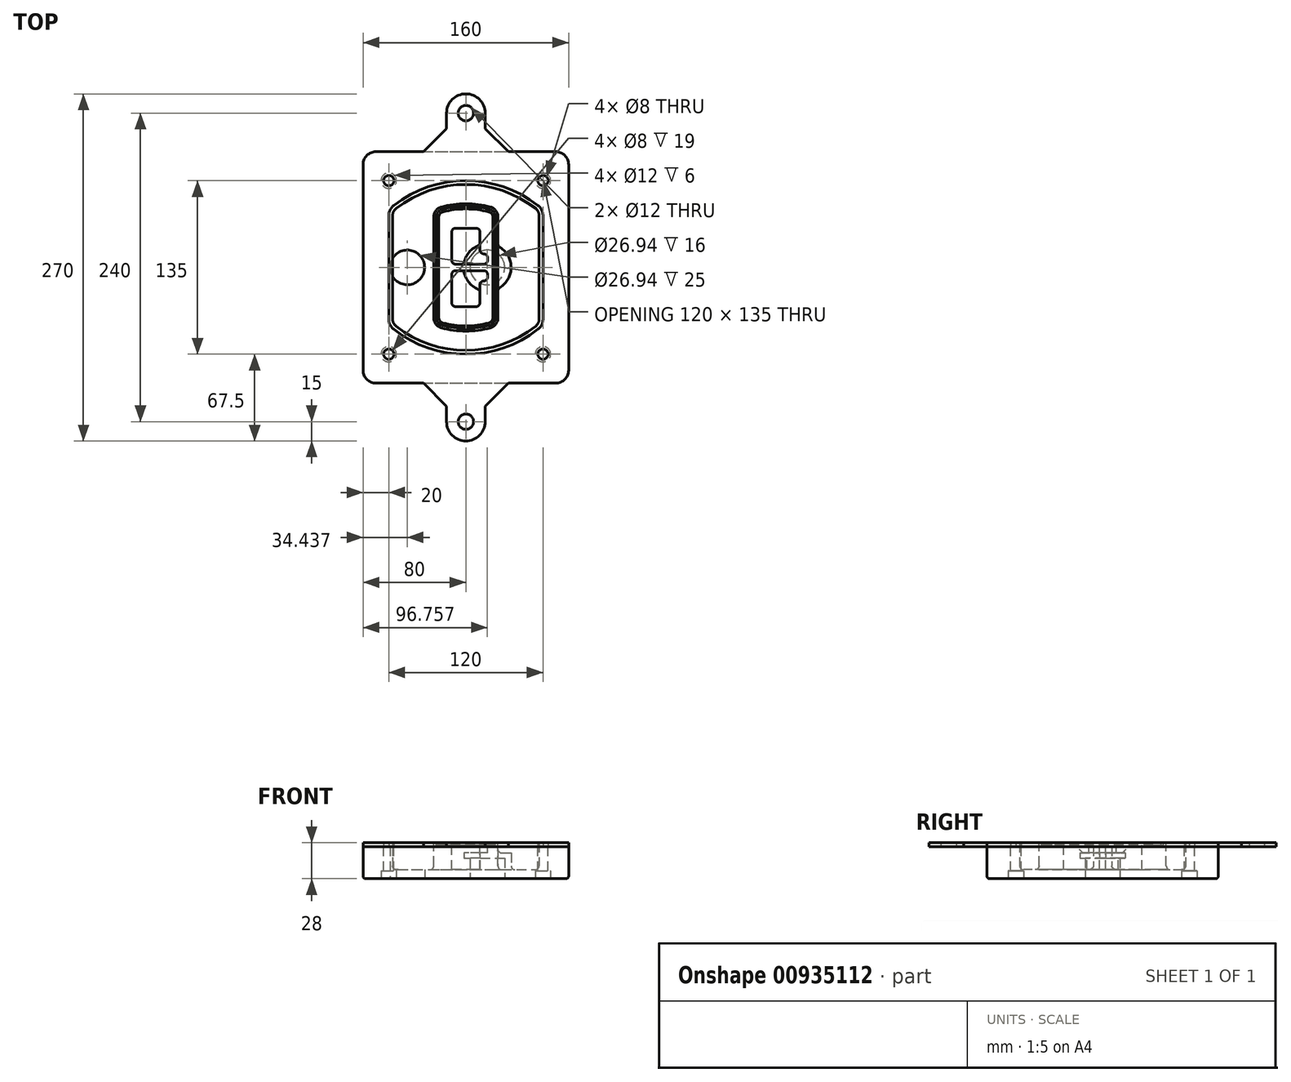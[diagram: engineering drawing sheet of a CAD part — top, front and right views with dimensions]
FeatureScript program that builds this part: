
annotation { "Feature Type Name" : "Feature", "Feature Type Description" : "" }
export const myFeature = defineFeature(function(context is Context, id is Id, definition is map)
    precondition{}
    {
        {
            var Q0;
            Q0=qCreatedBy(makeId("Top.planeOp"),FACE);
            var sketch = newSketch(context, id + "F0", { "sketchPlane" : qUnion([Q0])});
            skPoint(sketch, "E0.rect.middle", {"position": v(0, 0) * mm});
            skLineSegment(sketch, "E1.bottom", {"start": v(-70, -90) * mm, "end": v(70, -90) * mm});
            skLineSegment(sketch, "E1.top", {"start": v(-70, 90) * mm, "end": v(70, 90) * mm});
            skLineSegment(sketch, "E1.left", {"start": v(-80, -80) * mm, "end": v(-80, 80) * mm});
            skLineSegment(sketch, "E1.right", {"start": v(80, -80) * mm, "end": v(80, 80) * mm});
            skLineSegment(sketch, "E2", {"start": v(-80, 90) * mm, "end": v(80, -90) * mm, "construction": true});
            skLineSegment(sketch, "E3", {"start": v(80, 90) * mm, "end": v(-80, -90) * mm, "construction": true});
            skCircle(sketch, "E4", {"center": v(-60, 67.5) * mm, "radius": 4 * mm});
            skCircle(sketch, "E5", {"center": v(60, 67.5) * mm, "radius": 4 * mm});
            skCircle(sketch, "E6", {"center": v(60, -67.5) * mm, "radius": 4 * mm});
            skCircle(sketch, "E7", {"center": v(-60, -67.5) * mm, "radius": 4 * mm});
            skLineSegment(sketch, "E8", {"start": v(-60, 67.5) * mm, "end": v(60, 67.5) * mm, "construction": true});
            skLineSegment(sketch, "E9", {"start": v(60, 67.5) * mm, "end": v(60, -67.5) * mm, "construction": true});
            skLineSegment(sketch, "E10", {"start": v(60, -67.5) * mm, "end": v(-60, -67.5) * mm, "construction": true});
            skLineSegment(sketch, "E11", {"start": v(-60, -67.5) * mm, "end": v(-60, 67.5) * mm, "construction": true});
            skLineSegment(sketch, "E12", {"start": v(-60, 40.3) * mm, "end": v(-60, -40.3) * mm});
            skLineSegment(sketch, "E13", {"start": v(60, 40.3) * mm, "end": v(60, -40.3) * mm});
            skArc(sketch, "E14", {"start": v(56.15, 48.18) * mm, "mid": v(0, 67.5) * mm, "end": v(-56.15, 48.18) * mm});
            skArc(sketch, "E15", {"start": v(-56.15, -48.18) * mm, "mid": v(0, -67.5) * mm, "end": v(56.15, -48.18) * mm});
            skLineSegment(sketch, "E16", {"start": v(-60, 0) * mm, "end": v(60, 0) * mm, "construction": true});
            skPoint(sketch, "E17.visualSharp", {"position": v(-60, -45) * mm});
            skArc(sketch, "E17.filletArc", {"start": v(-60, -40.3) * mm, "mid": v(-58.99, -44.68) * mm, "end": v(-56.15, -48.18) * mm});
            skPoint(sketch, "E18.visualSharp", {"position": v(-60, 45) * mm});
            skArc(sketch, "E18.filletArc", {"start": v(-56.15, 48.18) * mm, "mid": v(-58.99, 44.68) * mm, "end": v(-60, 40.3) * mm});
            skPoint(sketch, "E19.visualSharp", {"position": v(60, 45) * mm});
            skArc(sketch, "E19.filletArc", {"start": v(60, 40.3) * mm, "mid": v(58.99, 44.68) * mm, "end": v(56.15, 48.18) * mm});
            skPoint(sketch, "E20.visualSharp", {"position": v(60, -45) * mm});
            skArc(sketch, "E20.filletArc", {"start": v(56.15, -48.18) * mm, "mid": v(58.99, -44.68) * mm, "end": v(60, -40.3) * mm});
            skPoint(sketch, "E21.visualSharp", {"position": v(-80, 90) * mm});
            skArc(sketch, "E21.filletArc", {"start": v(-70, 90) * mm, "mid": v(-77.07, 87.07) * mm, "end": v(-80, 80) * mm});
            skPoint(sketch, "E22.visualSharp", {"position": v(80, 90) * mm});
            skArc(sketch, "E22.filletArc", {"start": v(80, 80) * mm, "mid": v(77.07, 87.07) * mm, "end": v(70, 90) * mm});
            skPoint(sketch, "E23.visualSharp", {"position": v(80, -90) * mm});
            skArc(sketch, "E23.filletArc", {"start": v(70, -90) * mm, "mid": v(77.07, -87.07) * mm, "end": v(80, -80) * mm});
            skPoint(sketch, "E24.visualSharp", {"position": v(-80, -90) * mm});
            skArc(sketch, "E24.filletArc", {"start": v(-80, -80) * mm, "mid": v(-77.07, -87.07) * mm, "end": v(-70, -90) * mm});
            skArc(sketch, "E25.0", {"start": v(57, 40.3) * mm, "mid": v(56.3, 43.36) * mm, "end": v(54.3, 45.81) * mm});
            skLineSegment(sketch, "E25.1", {"start": v(57, 40.3) * mm, "end": v(57, -40.3) * mm});
            skArc(sketch, "E25.2", {"start": v(54.3, -45.81) * mm, "mid": v(56.3, -43.36) * mm, "end": v(57, -40.3) * mm});
            skArc(sketch, "E25.3", {"start": v(-54.3, -45.81) * mm, "mid": v(0, -64.5) * mm, "end": v(54.3, -45.81) * mm});
            skArc(sketch, "E25.4", {"start": v(-57, -40.3) * mm, "mid": v(-56.3, -43.36) * mm, "end": v(-54.3, -45.81) * mm});
            skArc(sketch, "E25.5", {"start": v(54.3, 45.81) * mm, "mid": v(0, 64.5) * mm, "end": v(-54.3, 45.81) * mm});
            skLineSegment(sketch, "E25.6", {"start": v(-57, 40.3) * mm, "end": v(-57, -40.3) * mm});
            skArc(sketch, "E25.7", {"start": v(-54.3, 45.81) * mm, "mid": v(-56.3, 43.36) * mm, "end": v(-57, 40.3) * mm});
            skArc(sketch, "E26.0", {"start": v(-58.62, 51.33) * mm, "mid": v(-62.58, 46.43) * mm, "end": v(-64, 40.3) * mm});
            skArc(sketch, "E26.1", {"start": v(58.62, 51.33) * mm, "mid": v(0, 71.5) * mm, "end": v(-58.62, 51.33) * mm});
            skArc(sketch, "E26.2", {"start": v(64, 40.3) * mm, "mid": v(62.58, 46.43) * mm, "end": v(58.62, 51.33) * mm});
            skLineSegment(sketch, "E26.3", {"start": v(64, 40.3) * mm, "end": v(64, -40.3) * mm});
            skArc(sketch, "E26.4", {"start": v(58.62, -51.33) * mm, "mid": v(62.58, -46.43) * mm, "end": v(64, -40.3) * mm});
            skLineSegment(sketch, "E26.5", {"start": v(-64, 40.3) * mm, "end": v(-64, -40.3) * mm});
            skArc(sketch, "E26.6", {"start": v(-58.62, -51.33) * mm, "mid": v(0, -71.5) * mm, "end": v(58.62, -51.33) * mm});
            skArc(sketch, "E26.7", {"start": v(-64, -40.3) * mm, "mid": v(-62.58, -46.43) * mm, "end": v(-58.62, -51.33) * mm});
            skSolve(sketch);
        }
        {
            var Q0;
            Q0=makeQuery(id+"F0.imprint","IMPRINT",FACE,{"disambiguationData":[TD([[makeQuery(id+"F0.imprint","IMPRINT",EDGE,{"derivedFrom":sQuery(id+"F0.wireOp",EDGE,"E1.bottom")}),1.0]])]});
            var Q1;
            Q1=makeQuery(id+"F0.imprint","IMPRINT",FACE,{"disambiguationData":[TD([[makeQuery(id+"F0.imprint","IMPRINT",EDGE,{"derivedFrom":sQuery(id+"F0.wireOp",EDGE,"E12")}),1.0]])]});
            var Q2;
            Q2=makeQuery(id+"F0.imprint","IMPRINT",FACE,{"disambiguationData":[TD([[makeQuery(id+"F0.imprint","IMPRINT",EDGE,{"derivedFrom":sQuery(id+"F0.wireOp",EDGE,"E25.0")}),1.0]])]});
            var Q3;
            Q3=makeQuery(id+"F0.imprint","IMPRINT",FACE,{"disambiguationData":[TD([[makeQuery(id+"F0.imprint","IMPRINT",EDGE,{"derivedFrom":sQuery(id+"F0.wireOp",EDGE,"E12")}),-1.0]])]});
            extrude(context, id + "F1", {"entities" : qUnion([Q0, Q1, Q2, Q3]), "oppositeDirection" : true, "depth" : 25 * mm, "offsetDistance" : 25 * mm});
        }
        {
            var Q0;
            Q0=makeQuery(id+"F0.imprint","IMPRINT",FACE,{"disambiguationData":[TD([[makeQuery(id+"F0.imprint","IMPRINT",EDGE,{"derivedFrom":sQuery(id+"F0.wireOp",EDGE,"E12")}),1.0]])]});
            extrude(context, id + "F2", {"entities" : qUnion([Q0]), "operationType" : NewBodyOperationType.ADD, "depth" : 3 * mm});
        }
        {
            var Q0;
            Q0=makeQuery(id+"F0.imprint","IMPRINT",FACE,{"disambiguationData":[TD([[makeQuery(id+"F0.imprint","IMPRINT",EDGE,{"derivedFrom":sQuery(id+"F0.wireOp",EDGE,"E25.0")}),1.0]])]});
            extrude(context, id + "F3", {"entities" : qUnion([Q0]), "operationType" : NewBodyOperationType.REMOVE, "oppositeDirection" : true, "depth" : 18 * mm});
        }
        {
            var Q0;
            Q0=makeQuery(id+"F2.opExtrude","CAP_FACE",FACE,{"disambiguationData":[OSD([sQuery(id+"F0.wireOp",EDGE,"E12"),sQuery(id+"F0.wireOp",EDGE,"E13"),sQuery(id+"F0.wireOp",EDGE,"E14"),sQuery(id+"F0.wireOp",EDGE,"E15"),sQuery(id+"F0.wireOp",EDGE,"E17.filletArc"),sQuery(id+"F0.wireOp",EDGE,"E18.filletArc"),sQuery(id+"F0.wireOp",EDGE,"E19.filletArc"),sQuery(id+"F0.wireOp",EDGE,"E20.filletArc"),sQuery(id+"F0.wireOp",EDGE,"E25.0"),sQuery(id+"F0.wireOp",EDGE,"E25.1"),sQuery(id+"F0.wireOp",EDGE,"E25.2"),sQuery(id+"F0.wireOp",EDGE,"E25.3"),sQuery(id+"F0.wireOp",EDGE,"E25.4"),sQuery(id+"F0.wireOp",EDGE,"E25.5"),sQuery(id+"F0.wireOp",EDGE,"E25.6"),sQuery(id+"F0.wireOp",EDGE,"E25.7")])],"isStart":false});
            var sketch = newSketch(context, id + "F4", { "sketchPlane" : qUnion([Q0])});
            skArc(sketch, "E27.0", {"start": v(-19.08, -46.97) * mm, "mid": v(0, -49.5) * mm, "end": v(19.08, -46.97) * mm});
            skArc(sketch, "E28.0", {"start": v(19.08, 46.97) * mm, "mid": v(0, 49.5) * mm, "end": v(-19.08, 46.97) * mm});
            skLineSegment(sketch, "E29", {"start": v(-25, 39.25) * mm, "end": v(-25, -39.25) * mm});
            skLineSegment(sketch, "E30", {"start": v(25, 39.25) * mm, "end": v(25, -39.25) * mm});
            skLineSegment(sketch, "E31", {"start": v(-25, 45.1) * mm, "end": v(25, 45.1) * mm, "construction": true});
            skLineSegment(sketch, "E32", {"start": v(-25, -45.1) * mm, "end": v(25, -45.1) * mm, "construction": true});
            skPoint(sketch, "E33.visualSharp", {"position": v(-25, 45.1) * mm});
            skArc(sketch, "E33.filletArc", {"start": v(-19.08, 46.97) * mm, "mid": v(-23.35, 44.11) * mm, "end": v(-25, 39.25) * mm});
            skPoint(sketch, "E34.visualSharp", {"position": v(25, 45.1) * mm});
            skArc(sketch, "E34.filletArc", {"start": v(25, 39.25) * mm, "mid": v(23.35, 44.11) * mm, "end": v(19.08, 46.97) * mm});
            skPoint(sketch, "E35.visualSharp", {"position": v(25, -45.1) * mm});
            skArc(sketch, "E35.filletArc", {"start": v(19.08, -46.97) * mm, "mid": v(23.35, -44.11) * mm, "end": v(25, -39.25) * mm});
            skPoint(sketch, "E36.visualSharp", {"position": v(-25, -45.1) * mm});
            skArc(sketch, "E36.filletArc", {"start": v(-25, -39.25) * mm, "mid": v(-23.35, -44.11) * mm, "end": v(-19.08, -46.97) * mm});
            skArc(sketch, "E37.0", {"start": v(54.3, 45.81) * mm, "mid": v(0, 64.5) * mm, "end": v(-54.3, 45.81) * mm});
            skArc(sketch, "E37.1", {"start": v(-54.3, 45.81) * mm, "mid": v(-56.3, 43.36) * mm, "end": v(-57, 40.3) * mm});
            skLineSegment(sketch, "E37.2", {"start": v(-57, 40.3) * mm, "end": v(-57, -40.3) * mm});
            skArc(sketch, "E37.3", {"start": v(-57, -40.3) * mm, "mid": v(-56.3, -43.36) * mm, "end": v(-54.3, -45.81) * mm});
            skArc(sketch, "E37.4", {"start": v(-54.3, -45.81) * mm, "mid": v(0, -64.5) * mm, "end": v(54.3, -45.81) * mm});
            skArc(sketch, "E37.5", {"start": v(54.3, -45.81) * mm, "mid": v(56.3, -43.36) * mm, "end": v(57, -40.3) * mm});
            skLineSegment(sketch, "E37.6", {"start": v(57, 40.3) * mm, "end": v(57, -40.3) * mm});
            skArc(sketch, "E37.7", {"start": v(57, 40.3) * mm, "mid": v(56.3, 43.36) * mm, "end": v(54.3, 45.81) * mm});
            skLineSegment(sketch, "E38.0", {"start": v(23, 39.25) * mm, "end": v(23, -39.25) * mm});
            skArc(sketch, "E38.1", {"start": v(18.56, -45.04) * mm, "mid": v(21.76, -42.9) * mm, "end": v(23, -39.25) * mm});
            skArc(sketch, "E38.2", {"start": v(-18.56, -45.04) * mm, "mid": v(0, -47.5) * mm, "end": v(18.56, -45.04) * mm});
            skArc(sketch, "E38.3", {"start": v(-23, -39.25) * mm, "mid": v(-21.76, -42.9) * mm, "end": v(-18.56, -45.04) * mm});
            skLineSegment(sketch, "E38.4", {"start": v(-23, 39.25) * mm, "end": v(-23, -39.25) * mm});
            skArc(sketch, "E38.5", {"start": v(23, 39.25) * mm, "mid": v(21.76, 42.9) * mm, "end": v(18.56, 45.04) * mm});
            skArc(sketch, "E38.6", {"start": v(-18.56, 45.04) * mm, "mid": v(-21.76, 42.9) * mm, "end": v(-23, 39.25) * mm});
            skArc(sketch, "E38.7", {"start": v(18.56, 45.04) * mm, "mid": v(0, 47.5) * mm, "end": v(-18.56, 45.04) * mm});
            skArc(sketch, "E39.0", {"start": v(21, 39.25) * mm, "mid": v(20.18, 41.68) * mm, "end": v(18.04, 43.1) * mm});
            skLineSegment(sketch, "E39.1", {"start": v(21, 39.25) * mm, "end": v(21, -39.25) * mm});
            skArc(sketch, "E39.2", {"start": v(18.04, -43.1) * mm, "mid": v(20.18, -41.68) * mm, "end": v(21, -39.25) * mm});
            skArc(sketch, "E39.3", {"start": v(-18.04, -43.1) * mm, "mid": v(0, -45.5) * mm, "end": v(18.04, -43.1) * mm});
            skArc(sketch, "E39.4", {"start": v(-21, -39.25) * mm, "mid": v(-20.18, -41.68) * mm, "end": v(-18.04, -43.1) * mm});
            skArc(sketch, "E39.5", {"start": v(18.04, 43.1) * mm, "mid": v(0, 45.5) * mm, "end": v(-18.04, 43.1) * mm});
            skLineSegment(sketch, "E39.6", {"start": v(-21, 39.25) * mm, "end": v(-21, -39.25) * mm});
            skArc(sketch, "E39.7", {"start": v(-18.04, 43.1) * mm, "mid": v(-20.18, 41.68) * mm, "end": v(-21, 39.25) * mm});
            skLineSegment(sketch, "E40", {"start": v(-25, 0) * mm, "end": v(25, 0) * mm, "construction": true});
            skLineSegment(sketch, "E41", {"start": v(-11, 5.5) * mm, "end": v(-11, 27.5) * mm});
            skLineSegment(sketch, "E42", {"start": v(-8, 30.5) * mm, "end": v(8, 30.5) * mm});
            skLineSegment(sketch, "E43", {"start": v(11, 27.5) * mm, "end": v(11, 13.5) * mm});
            skLineSegment(sketch, "E44", {"start": v(14, 10.5) * mm, "end": v(14, 10.5) * mm});
            skLineSegment(sketch, "E45", {"start": v(17, 7.5) * mm, "end": v(17, 5.5) * mm});
            skLineSegment(sketch, "E46", {"start": v(14, 2.5) * mm, "end": v(-8, 2.5) * mm});
            skPoint(sketch, "E47.visualSharp", {"position": v(-11, 30.5) * mm});
            skArc(sketch, "E47.filletArc", {"start": v(-8, 30.5) * mm, "mid": v(-10.12, 29.62) * mm, "end": v(-11, 27.5) * mm});
            skPoint(sketch, "E48.visualSharp", {"position": v(11, 30.5) * mm});
            skArc(sketch, "E48.filletArc", {"start": v(11, 27.5) * mm, "mid": v(10.12, 29.62) * mm, "end": v(8, 30.5) * mm});
            skPoint(sketch, "E49.visualSharp", {"position": v(11, 10.5) * mm});
            skArc(sketch, "E49.filletArc", {"start": v(11, 13.5) * mm, "mid": v(11.88, 11.38) * mm, "end": v(14, 10.5) * mm});
            skPoint(sketch, "E50.visualSharp", {"position": v(17, 10.5) * mm});
            skArc(sketch, "E50.filletArc", {"start": v(17, 7.5) * mm, "mid": v(16.12, 9.62) * mm, "end": v(14, 10.5) * mm});
            skPoint(sketch, "E51.visualSharp", {"position": v(17, 2.5) * mm});
            skArc(sketch, "E51.filletArc", {"start": v(14, 2.5) * mm, "mid": v(16.12, 3.38) * mm, "end": v(17, 5.5) * mm});
            skPoint(sketch, "E52.visualSharp", {"position": v(-11, 2.5) * mm});
            skArc(sketch, "E52.filletArc", {"start": v(-11, 5.5) * mm, "mid": v(-10.12, 3.38) * mm, "end": v(-8, 2.5) * mm});
            skLineSegment(sketch, "E53.0.MirrorCS", {"start": v(14, -2.5) * mm, "end": v(-8, -2.5) * mm});
            skArc(sketch, "E54.0.MirrorCS", {"start": v(-11, -5.5) * mm, "mid": v(-10.12, -3.38) * mm, "end": v(-8, -2.5) * mm});
            skLineSegment(sketch, "E55.0.MirrorCS", {"start": v(-11, -5.5) * mm, "end": v(-11, -27.5) * mm});
            skArc(sketch, "E56.0.MirrorCS", {"start": v(-8, -30.5) * mm, "mid": v(-10.12, -29.62) * mm, "end": v(-11, -27.5) * mm});
            skLineSegment(sketch, "E57.0.MirrorCS", {"start": v(-8, -30.5) * mm, "end": v(8, -30.5) * mm});
            skArc(sketch, "E58.0.MirrorCS", {"start": v(11, -27.5) * mm, "mid": v(10.12, -29.62) * mm, "end": v(8, -30.5) * mm});
            skLineSegment(sketch, "E59.0.MirrorCS", {"start": v(11, -27.5) * mm, "end": v(11, -13.5) * mm});
            skArc(sketch, "E60.0.MirrorCS", {"start": v(11, -13.5) * mm, "mid": v(11.88, -11.38) * mm, "end": v(14, -10.5) * mm});
            skArc(sketch, "E61.0.MirrorCS", {"start": v(17, -7.5) * mm, "mid": v(16.12, -9.62) * mm, "end": v(14, -10.5) * mm});
            skLineSegment(sketch, "E62.0.MirrorCS", {"start": v(17, -7.5) * mm, "end": v(17, -5.5) * mm});
            skArc(sketch, "E63.0.MirrorCS", {"start": v(14, -2.5) * mm, "mid": v(16.12, -3.38) * mm, "end": v(17, -5.5) * mm});
            skSolve(sketch);
        }
        {
            var Q0;
            Q0=makeQuery(id+"F4.imprint","IMPRINT",FACE,{"disambiguationData":[TD([[makeQuery(id+"F4.imprint","IMPRINT",EDGE,{"derivedFrom":sQuery(id+"F4.wireOp",EDGE,"E27.0")}),1.0]])]});
            var Q1;
            Q1=makeQuery(id+"F4.imprint","IMPRINT",FACE,{"disambiguationData":[TD([[makeQuery(id+"F4.imprint","IMPRINT",EDGE,{"derivedFrom":sQuery(id+"F4.wireOp",EDGE,"E38.0")}),-1.0]])]});
            var Q2;
            Q2=makeQuery(id+"F4.imprint","IMPRINT",FACE,{"disambiguationData":[TD([[makeQuery(id+"F4.imprint","IMPRINT",EDGE,{"derivedFrom":sQuery(id+"F4.wireOp",EDGE,"E39.0")}),1.0]])]});
            extrude(context, id + "F5", {"entities" : qUnion([Q0, Q1, Q2]), "operationType" : NewBodyOperationType.ADD, "endBound" : BoundingType.UP_TO_NEXT, "oppositeDirection" : true, "depth" : 25 * mm});
        }
        {
            var Q0;
            Q0=makeQuery(id+"F4.imprint","IMPRINT",FACE,{"disambiguationData":[TD([[makeQuery(id+"F4.imprint","IMPRINT",EDGE,{"derivedFrom":sQuery(id+"F4.wireOp",EDGE,"E38.0")}),-1.0]])]});
            extrude(context, id + "F6", {"entities" : qUnion([Q0]), "operationType" : NewBodyOperationType.REMOVE, "oppositeDirection" : true, "depth" : 2 * mm});
        }
        {
            var Q0;
            Q0=makeQuery(id+"F1.opExtrude","CAP_FACE",FACE,{"disambiguationData":[OSD([sQuery(id+"F0.wireOp",EDGE,"E1.bottom"),sQuery(id+"F0.wireOp",EDGE,"E1.top"),sQuery(id+"F0.wireOp",EDGE,"E1.left"),sQuery(id+"F0.wireOp",EDGE,"E1.right"),sQuery(id+"F0.wireOp",EDGE,"E4"),sQuery(id+"F0.wireOp",EDGE,"E5"),sQuery(id+"F0.wireOp",EDGE,"E6"),sQuery(id+"F0.wireOp",EDGE,"E7"),sQuery(id+"F0.wireOp",EDGE,"E21.filletArc"),sQuery(id+"F0.wireOp",EDGE,"E22.filletArc"),sQuery(id+"F0.wireOp",EDGE,"E23.filletArc"),sQuery(id+"F0.wireOp",EDGE,"E24.filletArc")])],"isStart":false});
            var sketch = newSketch(context, id + "F7", { "sketchPlane" : qUnion([Q0])});
            skCircle(sketch, "E64", {"center": v(16.76, 0) * mm, "radius": 13.47 * mm});
            skCircle(sketch, "E65", {"center": v(-45.56, 0) * mm, "radius": 13.47 * mm});
            skLineSegment(sketch, "E66", {"start": v(80, 0) * mm, "end": v(-80, 0) * mm});
            skCircle(sketch, "E67", {"center": v(16.76, 0) * mm, "radius": 18.47 * mm});
            skCircle(sketch, "E68", {"center": v(60, -67.5) * mm, "radius": 6 * mm});
            skCircle(sketch, "E69", {"center": v(-60, -67.5) * mm, "radius": 6 * mm});
            skCircle(sketch, "E70", {"center": v(-60, 67.5) * mm, "radius": 6 * mm});
            skCircle(sketch, "E71", {"center": v(60, 67.5) * mm, "radius": 6 * mm});
            skSolve(sketch);
        }
        {
            var Q0;
            {var subQ1=sQuery(id+"F7.wireOp",EDGE,"E66");var subQ4=sQuery(id+"F7.wireOp",EDGE,"E64");var subQ6=makeQuery(id+"F7.imprint","INTERSECT",VERTEX,{"disambiguationData":[OD(0.0)],"derivedFrom":[subQ4,subQ1]});Q0=makeQuery(id+"F7.imprint","IMPRINT",FACE,{"disambiguationData":[TD([[makeQuery(id+"F7.imprint","IMPRINT",EDGE,{"disambiguationData":[TD([[subQ6,-1.0]])],"derivedFrom":subQ4}),-1.0]])]});}
            var Q1;
            {var subQ0=sQuery(id+"F7.wireOp",EDGE,"E66");var subQ1=sQuery(id+"F7.wireOp",EDGE,"E64");var subQ3=makeQuery(id+"F7.imprint","INTERSECT",VERTEX,{"disambiguationData":[OD(0.0)],"derivedFrom":[subQ1,subQ0]});Q1=makeQuery(id+"F7.imprint","IMPRINT",FACE,{"disambiguationData":[TD([[makeQuery(id+"F7.imprint","IMPRINT",EDGE,{"disambiguationData":[TD([[subQ3,-1.0]])],"derivedFrom":subQ1}),1.0]])]});}
            var Q2;
            {var subQ0=sQuery(id+"F7.wireOp",EDGE,"E66");var subQ1=sQuery(id+"F7.wireOp",EDGE,"E64");var subQ3=makeQuery(id+"F7.imprint","INTERSECT",VERTEX,{"disambiguationData":[OD(0.0)],"derivedFrom":[subQ1,subQ0]});Q2=makeQuery(id+"F7.imprint","IMPRINT",FACE,{"disambiguationData":[TD([[makeQuery(id+"F7.imprint","IMPRINT",EDGE,{"disambiguationData":[TD([[subQ3,1.0]])],"derivedFrom":subQ1}),1.0]])]});}
            var Q3;
            {var subQ1=sQuery(id+"F7.wireOp",EDGE,"E66");var subQ4=sQuery(id+"F7.wireOp",EDGE,"E64");var subQ6=makeQuery(id+"F7.imprint","INTERSECT",VERTEX,{"disambiguationData":[OD(0.0)],"derivedFrom":[subQ4,subQ1]});Q3=makeQuery(id+"F7.imprint","IMPRINT",FACE,{"disambiguationData":[TD([[makeQuery(id+"F7.imprint","IMPRINT",EDGE,{"disambiguationData":[TD([[subQ6,1.0]])],"derivedFrom":subQ4}),-1.0]])]});}
            extrude(context, id + "F8", {"entities" : qUnion([Q0, Q1, Q2, Q3]), "operationType" : NewBodyOperationType.ADD, "oppositeDirection" : true, "depth" : 20 * mm});
        }
        {
            var Q0;
            {var subQ0=sQuery(id+"F7.wireOp",EDGE,"E66");var subQ1=sQuery(id+"F7.wireOp",EDGE,"E64");var subQ3=makeQuery(id+"F7.imprint","INTERSECT",VERTEX,{"disambiguationData":[OD(0.0)],"derivedFrom":[subQ1,subQ0]});Q0=makeQuery(id+"F7.imprint","IMPRINT",FACE,{"disambiguationData":[TD([[makeQuery(id+"F7.imprint","IMPRINT",EDGE,{"disambiguationData":[TD([[subQ3,-1.0]])],"derivedFrom":subQ1}),1.0]])]});}
            var Q1;
            {var subQ0=sQuery(id+"F7.wireOp",EDGE,"E66");var subQ1=sQuery(id+"F7.wireOp",EDGE,"E64");var subQ3=makeQuery(id+"F7.imprint","INTERSECT",VERTEX,{"disambiguationData":[OD(0.0)],"derivedFrom":[subQ1,subQ0]});Q1=makeQuery(id+"F7.imprint","IMPRINT",FACE,{"disambiguationData":[TD([[makeQuery(id+"F7.imprint","IMPRINT",EDGE,{"disambiguationData":[TD([[subQ3,1.0]])],"derivedFrom":subQ1}),1.0]])]});}
            extrude(context, id + "F9", {"entities" : qUnion([Q0, Q1]), "operationType" : NewBodyOperationType.REMOVE, "oppositeDirection" : true, "depth" : 16 * mm});
        }
        {
            var Q0;
            {var subQ0=sQuery(id+"F7.wireOp",EDGE,"E66");var subQ1=sQuery(id+"F7.wireOp",EDGE,"E65");var subQ3=makeQuery(id+"F7.imprint","INTERSECT",VERTEX,{"disambiguationData":[OD(0.0)],"derivedFrom":[subQ1,subQ0]});Q0=makeQuery(id+"F7.imprint","IMPRINT",FACE,{"disambiguationData":[TD([[makeQuery(id+"F7.imprint","IMPRINT",EDGE,{"disambiguationData":[TD([[subQ3,-1.0]])],"derivedFrom":subQ1}),1.0]])]});}
            var Q1;
            {var subQ0=sQuery(id+"F7.wireOp",EDGE,"E66");var subQ1=sQuery(id+"F7.wireOp",EDGE,"E65");var subQ3=makeQuery(id+"F7.imprint","INTERSECT",VERTEX,{"disambiguationData":[OD(0.0)],"derivedFrom":[subQ1,subQ0]});Q1=makeQuery(id+"F7.imprint","IMPRINT",FACE,{"disambiguationData":[TD([[makeQuery(id+"F7.imprint","IMPRINT",EDGE,{"disambiguationData":[TD([[subQ3,1.0]])],"derivedFrom":subQ1}),1.0]])]});}
            extrude(context, id + "F10", {"entities" : qUnion([Q0, Q1]), "operationType" : NewBodyOperationType.REMOVE, "oppositeDirection" : true, "depth" : 25 * mm});
        }
        {
            var Q0;
            Q0=makeQuery(id+"F7.imprint","IMPRINT",FACE,{"disambiguationData":[TD([[makeQuery(id+"F7.imprint","IMPRINT",EDGE,{"derivedFrom":sQuery(id+"F7.wireOp",EDGE,"E68")}),1.0]])]});
            var Q1;
            Q1=makeQuery(id+"F7.imprint","IMPRINT",FACE,{"disambiguationData":[TD([[makeQuery(id+"F7.imprint","IMPRINT",EDGE,{"derivedFrom":makeQuery(id+"F1.opExtrude","CAP_EDGE",EDGE,{"disambiguationData":[OSD([sQuery(id+"F0.wireOp",EDGE,"E5")])],"isStart":false})}),-1.0]])]});
            var Q2;
            Q2=makeQuery(id+"F7.imprint","IMPRINT",FACE,{"disambiguationData":[TD([[makeQuery(id+"F7.imprint","IMPRINT",EDGE,{"derivedFrom":sQuery(id+"F7.wireOp",EDGE,"E69")}),1.0]])]});
            var Q3;
            Q3=makeQuery(id+"F7.imprint","IMPRINT",FACE,{"disambiguationData":[TD([[makeQuery(id+"F7.imprint","IMPRINT",EDGE,{"derivedFrom":makeQuery(id+"F1.opExtrude","CAP_EDGE",EDGE,{"disambiguationData":[OSD([sQuery(id+"F0.wireOp",EDGE,"E4")])],"isStart":false})}),-1.0]])]});
            var Q4;
            Q4=makeQuery(id+"F7.imprint","IMPRINT",FACE,{"disambiguationData":[TD([[makeQuery(id+"F7.imprint","IMPRINT",EDGE,{"derivedFrom":sQuery(id+"F7.wireOp",EDGE,"E70")}),1.0]])]});
            var Q5;
            Q5=makeQuery(id+"F7.imprint","IMPRINT",FACE,{"disambiguationData":[TD([[makeQuery(id+"F7.imprint","IMPRINT",EDGE,{"derivedFrom":makeQuery(id+"F1.opExtrude","CAP_EDGE",EDGE,{"disambiguationData":[OSD([sQuery(id+"F0.wireOp",EDGE,"E7")])],"isStart":false})}),-1.0]])]});
            var Q6;
            Q6=makeQuery(id+"F7.imprint","IMPRINT",FACE,{"disambiguationData":[TD([[makeQuery(id+"F7.imprint","IMPRINT",EDGE,{"derivedFrom":sQuery(id+"F7.wireOp",EDGE,"E71")}),1.0]])]});
            var Q7;
            Q7=makeQuery(id+"F7.imprint","IMPRINT",FACE,{"disambiguationData":[TD([[makeQuery(id+"F7.imprint","IMPRINT",EDGE,{"derivedFrom":makeQuery(id+"F1.opExtrude","CAP_EDGE",EDGE,{"disambiguationData":[OSD([sQuery(id+"F0.wireOp",EDGE,"E6")])],"isStart":false})}),-1.0]])]});
            extrude(context, id + "F11", {"entities" : qUnion([Q0, Q1, Q2, Q3, Q4, Q5, Q6, Q7]), "operationType" : NewBodyOperationType.REMOVE, "oppositeDirection" : true, "depth" : 6 * mm});
        }
        {
            var Q0;
            Q0=makeQuery(id+"F9.boolean.opBoolean","COPY",FACE,{"derivedFrom":makeQuery(id+"F9.opExtrude","CAP_FACE",FACE,{"disambiguationData":[OSD([sQuery(id+"F7.wireOp",EDGE,"E64")])],"isStart":false})});
            var sketch = newSketch(context, id + "F12", { "sketchPlane" : qUnion([Q0])});
            skArc(sketch, "E72.0", {"start": v(11, 17.55) * mm, "mid": v(2.57, 11.82) * mm, "end": v(-1.54, 2.5) * mm});
            skArc(sketch, "E72.1", {"start": v(-1.54, -2.5) * mm, "mid": v(2.57, -11.82) * mm, "end": v(11, -17.55) * mm});
            skLineSegment(sketch, "E73", {"start": v(-1.54, -2.5) * mm, "end": v(14, -2.5) * mm});
            skLineSegment(sketch, "E74.0", {"start": v(14, 2.5) * mm, "end": v(-1.54, 2.5) * mm});
            skArc(sketch, "E74.1", {"start": v(14, 2.5) * mm, "mid": v(16.12, 3.38) * mm, "end": v(17, 5.5) * mm});
            skLineSegment(sketch, "E74.2", {"start": v(17, 7.5) * mm, "end": v(17, 5.5) * mm});
            skArc(sketch, "E74.3", {"start": v(17, 7.5) * mm, "mid": v(16.12, 9.62) * mm, "end": v(14, 10.5) * mm});
            skArc(sketch, "E74.4", {"start": v(11, 13.5) * mm, "mid": v(11.88, 11.38) * mm, "end": v(14, 10.5) * mm});
            skLineSegment(sketch, "E74.5", {"start": v(11, 17.55) * mm, "end": v(11, 13.5) * mm});
            skLineSegment(sketch, "E74.7", {"start": v(14, -2.5) * mm, "end": v(-1.54, -2.5) * mm});
            skArc(sketch, "E74.8", {"start": v(14, -2.5) * mm, "mid": v(16.12, -3.38) * mm, "end": v(17, -5.5) * mm});
            skLineSegment(sketch, "E74.9", {"start": v(17, -7.5) * mm, "end": v(17, -5.5) * mm});
            skArc(sketch, "E74.10", {"start": v(17, -7.5) * mm, "mid": v(16.12, -9.62) * mm, "end": v(14, -10.5) * mm});
            skArc(sketch, "E74.11", {"start": v(11, -13.5) * mm, "mid": v(11.88, -11.38) * mm, "end": v(14, -10.5) * mm});
            skLineSegment(sketch, "E74.12", {"start": v(11, -17.55) * mm, "end": v(11, -13.5) * mm});
            skPoint(sketch, "E75.orphan", {"position": v(11, -27.5) * mm});
            skPoint(sketch, "E76.orphan", {"position": v(-8, -2.5) * mm});
            skPoint(sketch, "E77.orphan", {"position": v(-8, 2.5) * mm});
            skPoint(sketch, "E78.orphan", {"position": v(11, 27.5) * mm});
            skSolve(sketch);
        }
        {
            var Q0;
            {var subQ7=sQuery(id+"F12.wireOp",EDGE,"E72.0");var subQ14=sQuery(id+"F12.wireOp",EDGE,"E72.1");var subQ16=sQuery(id+"F12.wireOp",EDGE,"E74.1");var subQ18=sQuery(id+"F12.wireOp",EDGE,"E74.8");Q0=qUnion([makeQuery(id+"F12.imprint","IMPRINT",FACE,{"disambiguationData":[TD([[makeQuery(id+"F12.imprint","IMPRINT",EDGE,{"derivedFrom":subQ7}),1.0]])]}),makeQuery(id+"F12.imprint","IMPRINT",FACE,{"disambiguationData":[TD([[makeQuery(id+"F12.imprint","IMPRINT",EDGE,{"derivedFrom":subQ14}),1.0]])]}),makeQuery(id+"F12.imprint","IMPRINT",FACE,{"disambiguationData":[TD([[makeQuery(id+"F12.imprint","IMPRINT",EDGE,{"derivedFrom":subQ16}),1.0]])]}),makeQuery(id+"F12.imprint","IMPRINT",FACE,{"disambiguationData":[TD([[makeQuery(id+"F12.imprint","IMPRINT",EDGE,{"derivedFrom":subQ18}),-1.0]])]})]);}
            var Q1;
            Q1=makeQuery(id+"F5.boolean.opBoolean","SPLIT",FACE,{"disambiguationData":[TD([makeQuery(id+"F5.opExtrude","SWEPT_FACE",FACE,{"disambiguationData":[OSD([sQuery(id+"F4.wireOp",EDGE,"E41")])]})])],"derivedFrom":makeQuery(id+"F3.boolean.opBoolean","COPY",FACE,{"derivedFrom":makeQuery(id+"F3.opExtrude","CAP_FACE",FACE,{"disambiguationData":[OSD([sQuery(id+"F0.wireOp",EDGE,"E25.0"),sQuery(id+"F0.wireOp",EDGE,"E25.1"),sQuery(id+"F0.wireOp",EDGE,"E25.2"),sQuery(id+"F0.wireOp",EDGE,"E25.3"),sQuery(id+"F0.wireOp",EDGE,"E25.4"),sQuery(id+"F0.wireOp",EDGE,"E25.5"),sQuery(id+"F0.wireOp",EDGE,"E25.6"),sQuery(id+"F0.wireOp",EDGE,"E25.7")])],"isStart":false})})});
            extrude(context, id + "F13", {"entities" : qUnion([Q0]), "operationType" : NewBodyOperationType.REMOVE, "endBound" : BoundingType.UP_TO_SURFACE, "endBoundEntityFace" : qUnion([Q1]), "depth" : 25 * mm});
        }
        {
            var Q0;
            Q0=makeQuery(id+"F3.boolean.opBoolean","COPY",EDGE,{"derivedFrom":makeQuery(id+"F3.opExtrude","CAP_EDGE",EDGE,{"disambiguationData":[OSD([sQuery(id+"F0.wireOp",EDGE,"E25.6")])],"isStart":false})});
            var Q1;
            Q1=makeQuery(id+"F8.boolean.opBoolean","INTERSECT",EDGE,{"derivedFrom":[makeQuery(id+"F5.opExtrude","SWEPT_FACE",FACE,{"disambiguationData":[OSD([sQuery(id+"F4.wireOp",EDGE,"E30")])]}),makeQuery(id+"F8.opExtrude","CAP_FACE",FACE,{"disambiguationData":[OSD([sQuery(id+"F7.wireOp",EDGE,"E67")])],"isStart":false})]});
            var Q2;
            Q2=makeQuery(id+"F8.boolean.opBoolean","INTERSECT",EDGE,{"disambiguationData":[OD(1.0)],"derivedFrom":[makeQuery(id+"F5.opExtrude","SWEPT_FACE",FACE,{"disambiguationData":[OSD([sQuery(id+"F4.wireOp",EDGE,"E30")])]}),makeQuery(id+"F8.opExtrude","SWEPT_FACE",FACE,{"disambiguationData":[OSD([sQuery(id+"F7.wireOp",EDGE,"E67")])]})]});
            var Q3;
            {var subQ0=sQuery(id+"F4.wireOp",EDGE,"E30");Q3=makeQuery(id+"F8.boolean.opBoolean","SPLIT",EDGE,{"disambiguationData":[TD([makeQuery(id+"F5.opExtrude","SWEPT_FACE",FACE,{"disambiguationData":[OSD([sQuery(id+"F4.wireOp",EDGE,"E35.filletArc")])]})])],"derivedFrom":makeQuery(id+"F5.opExtrude","CAP_EDGE",EDGE,{"disambiguationData":[OSD([subQ0])],"isStart":false})});}
            var Q4;
            {var subQ0=sQuery(id+"F0.wireOp",EDGE,"E25.7");var subQ1=sQuery(id+"F0.wireOp",EDGE,"E25.1");var subQ2=sQuery(id+"F0.wireOp",EDGE,"E25.6");var subQ3=sQuery(id+"F0.wireOp",EDGE,"E25.5");var subQ4=sQuery(id+"F0.wireOp",EDGE,"E25.4");var subQ5=sQuery(id+"F0.wireOp",EDGE,"E25.0");var subQ6=sQuery(id+"F0.wireOp",EDGE,"E25.2");var subQ7=sQuery(id+"F0.wireOp",EDGE,"E25.3");Q4=makeQuery(id+"F8.boolean.opBoolean","INTERSECT",EDGE,{"derivedFrom":[makeQuery(id+"F5.boolean.opBoolean","SPLIT",FACE,{"disambiguationData":[TD([makeQuery(id+"F2.opExtrude","SWEPT_FACE",FACE,{"disambiguationData":[OSD([subQ5])]})])],"derivedFrom":makeQuery(id+"F3.boolean.opBoolean","COPY",FACE,{"derivedFrom":makeQuery(id+"F3.opExtrude","CAP_FACE",FACE,{"disambiguationData":[OSD([subQ5,subQ1,subQ6,subQ7,subQ4,subQ3,subQ2,subQ0])],"isStart":false})})}),makeQuery(id+"F8.opExtrude","SWEPT_FACE",FACE,{"disambiguationData":[OSD([sQuery(id+"F7.wireOp",EDGE,"E67")])]})]});}
            var Q5;
            Q5=makeQuery(id+"F8.boolean.opBoolean","INTERSECT",EDGE,{"disambiguationData":[OD(0.0)],"derivedFrom":[makeQuery(id+"F5.opExtrude","SWEPT_FACE",FACE,{"disambiguationData":[OSD([sQuery(id+"F4.wireOp",EDGE,"E30")])]}),makeQuery(id+"F8.opExtrude","SWEPT_FACE",FACE,{"disambiguationData":[OSD([sQuery(id+"F7.wireOp",EDGE,"E67")])]})]});
            fillet(context, id + "F14", {"entities" : qUnion([Q0, Q1, Q2, Q3, Q4, Q5]), "radius" : 3 * mm, "tangentPropagation" : true, "allowEdgeOverflow" : false});
        }
        {
            var Q0;
            Q0=makeQuery(id+"F1.opExtrude","CAP_EDGE",EDGE,{"disambiguationData":[OSD([sQuery(id+"F0.wireOp",EDGE,"E1.bottom")])],"isStart":false});
            fillet(context, id + "F15", {"entities" : qUnion([Q0]), "radius" : 2 * mm, "tangentPropagation" : true, "allowEdgeOverflow" : false});
        }
        {
            var Q0;
            {var subQ0=sQuery(id+"F0.wireOp",EDGE,"E21.filletArc");var subQ1=sQuery(id+"F0.wireOp",EDGE,"E7");var subQ2=sQuery(id+"F0.wireOp",EDGE,"E6");var subQ3=sQuery(id+"F0.wireOp",EDGE,"E5");var subQ4=sQuery(id+"F0.wireOp",EDGE,"E4");var subQ5=sQuery(id+"F0.wireOp",EDGE,"E22.filletArc");var subQ6=sQuery(id+"F0.wireOp",EDGE,"E1.bottom");var subQ7=sQuery(id+"F0.wireOp",EDGE,"E1.right");var subQ8=sQuery(id+"F0.wireOp",EDGE,"E1.top");var subQ9=sQuery(id+"F0.wireOp",EDGE,"E1.left");var subQ10=sQuery(id+"F0.wireOp",EDGE,"E23.filletArc");var subQ11=sQuery(id+"F0.wireOp",EDGE,"E24.filletArc");Q0=makeQuery(id+"F2.boolean.opBoolean","SPLIT",FACE,{"disambiguationData":[TD([makeQuery(id+"F1.opExtrude","SWEPT_FACE",FACE,{"disambiguationData":[OSD([subQ6])]})])],"derivedFrom":makeQuery(id+"F1.opExtrude","CAP_FACE",FACE,{"disambiguationData":[OSD([subQ6,subQ8,subQ9,subQ7,subQ4,subQ3,subQ2,subQ1,subQ0,subQ5,subQ10,subQ11])],"isStart":true})});}
            var sketch = newSketch(context, id + "F16", { "sketchPlane" : qUnion([Q0])});
            skLineSegment(sketch, "E79", {"start": v(0, 90) * mm, "end": v(0, 120) * mm, "construction": true});
            skLineSegment(sketch, "E80", {"start": v(-33, 90) * mm, "end": v(-15, 108) * mm});
            skLineSegment(sketch, "E81", {"start": v(-15, 108) * mm, "end": v(-15, 120) * mm});
            skLineSegment(sketch, "E82.MirrorCS", {"start": v(33, 90) * mm, "end": v(15, 108) * mm});
            skLineSegment(sketch, "E83.MirrorCS", {"start": v(15, 108) * mm, "end": v(15, 120) * mm});
            skArc(sketch, "E84", {"start": v(15, 120) * mm, "mid": v(0, 135) * mm, "end": v(-15, 120) * mm});
            skCircle(sketch, "E85", {"center": v(0, 120) * mm, "radius": 6 * mm});
            skLineSegment(sketch, "E86", {"start": v(-80, 0) * mm, "end": v(80, 0) * mm, "construction": true});
            skLineSegment(sketch, "E87.MirrorCS", {"start": v(33, -90) * mm, "end": v(15, -108) * mm});
            skLineSegment(sketch, "E88.MirrorCS", {"start": v(15, -108) * mm, "end": v(15, -120) * mm});
            skArc(sketch, "E89.MirrorCS", {"start": v(15, -120) * mm, "mid": v(0, -135) * mm, "end": v(-15, -120) * mm});
            skLineSegment(sketch, "E90.MirrorCS", {"start": v(-15, -108) * mm, "end": v(-15, -120) * mm});
            skLineSegment(sketch, "E91.MirrorCS", {"start": v(-33, -90) * mm, "end": v(-15, -108) * mm});
            skCircle(sketch, "E92.MirrorC", {"center": v(0, -120) * mm, "radius": 6 * mm});
            skLineSegment(sketch, "E93.MirrorCS", {"start": v(0, -90) * mm, "end": v(0, -120) * mm, "construction": true});
            skSolve(sketch);
        }
        {
            var Q0;
            Q0=makeQuery(id+"F16.imprint","IMPRINT",FACE,{"disambiguationData":[TD([[makeQuery(id+"F16.imprint","IMPRINT",EDGE,{"derivedFrom":makeQuery(id+"F1.opExtrude","CAP_EDGE",EDGE,{"disambiguationData":[OSD([sQuery(id+"F0.wireOp",EDGE,"E1.left")])],"isStart":true})}),-1.0]])]});
            var Q1;
            {var subQ0=sQuery(id+"F16.wireOp",EDGE,"E87.MirrorCS");Q1=makeQuery(id+"F16.imprint","IMPRINT",FACE,{"disambiguationData":[TD([[makeQuery(id+"F16.imprint","IMPRINT",EDGE,{"derivedFrom":subQ0}),-1.0]])]});}
            var Q2;
            {var subQ1=sQuery(id+"F16.wireOp",EDGE,"E80");Q2=makeQuery(id+"F16.imprint","IMPRINT",FACE,{"disambiguationData":[TD([[makeQuery(id+"F16.imprint","IMPRINT",EDGE,{"derivedFrom":subQ1}),-1.0]])]});}
            var Q3;
            Q3=makeQuery(id+"F2.opExtrude","CAP_FACE",FACE,{"disambiguationData":[OSD([sQuery(id+"F0.wireOp",EDGE,"E12"),sQuery(id+"F0.wireOp",EDGE,"E13"),sQuery(id+"F0.wireOp",EDGE,"E14"),sQuery(id+"F0.wireOp",EDGE,"E15"),sQuery(id+"F0.wireOp",EDGE,"E17.filletArc"),sQuery(id+"F0.wireOp",EDGE,"E18.filletArc"),sQuery(id+"F0.wireOp",EDGE,"E19.filletArc"),sQuery(id+"F0.wireOp",EDGE,"E20.filletArc"),sQuery(id+"F0.wireOp",EDGE,"E25.0"),sQuery(id+"F0.wireOp",EDGE,"E25.1"),sQuery(id+"F0.wireOp",EDGE,"E25.2"),sQuery(id+"F0.wireOp",EDGE,"E25.3"),sQuery(id+"F0.wireOp",EDGE,"E25.4"),sQuery(id+"F0.wireOp",EDGE,"E25.5"),sQuery(id+"F0.wireOp",EDGE,"E25.6"),sQuery(id+"F0.wireOp",EDGE,"E25.7")])],"isStart":false});
            extrude(context, id + "F17", {"entities" : qUnion([Q0, Q1, Q2]), "endBound" : BoundingType.UP_TO_SURFACE, "depth" : 25 * mm, "endBoundEntityFace" : qUnion([Q3]), "offsetDistance" : 25 * mm});
        }
    });
